# Revit family: Scale-SR_Scales-SRV947-R-IFS
name_source: partatom
category: Specialty Equipment
units: mm (PartAtom-declared; Revit-internal decimal feet)

## family parameters
Always vertical = Yes
Cut with Voids When Loaded = No
OmniClass Number = 23.40.70.11.14.11
OmniClass Title = Medical Equipment
Part Type = Normal
Room Calculation Point = No
Round Connector Dimension = Use Diameter
Shared = No
Work Plane-Based = No

## types (9) — shared parameters
Accuracy = 0.2% +/- 2 Digits of Displayed Resolution
Assembly Code = E1020810
Auto Power Down = Approximately 120 Seconds
Averaging = Automatic Digital Filter
BIM Version = v3.1
BIM Version Available (Earliest) = 2017
Calibration = Traceable to NIST Standards
Default Elevation = 0"
Display Resolution = 0.2 lb / 0.1 kg
Manufacturer = SR Scales by SR Instruments, Inc.
Maximum Weight Capacity = 400 lbs or 182 kg
Platform Depth = 24"
Power Supply = Six (6) AA 1.5 Volt Alkaline Batteries
Product Brochure Link = https://srinstruments.com
Product Page URL = https://srinstruments.com
URL = http://www.srinstruments.com
Zero = One Button Operation Auto Zero

## per-type parameters (varying)
| type | Description | Display Type | Platform Height Position | Platform Size | Platform Width | Remote Display (Not Shown Graphically) | Show Display in Platform | Show Flush Mounted Wall Display | Show Recessed Pit Frame |
| SRV947IFS | 24" x 48" Portable (or Fixed) Platform Scale with Flush Wall Mounted Display | 1.0'' LCD Display with 5 Active Digits | 0" | "24'' x 48'' x 2" (61 cm x 122 cm x 5 cm)" | 48" | No | No | Yes | Yes |
| SRV947 | 24" x 48" Portable (or Fixed) Platform Scale with Display in Platform | 1.0'' LCD Display with 5 Active Digits | 2" | "24'' x 48'' x 2" (61 cm x 122 cm x 5 cm)" | 48" | No | Yes | No | No |
| SRV947R | 24" x 48" Portable (or Fixed) Platform Scale with Remote Display | 0.75'' LCD Display with 4.5 Active Digits | 2" | "24'' x 48'' x 2" (61 cm x 122 cm x 5 cm)" | 48" | Yes | No | No | No |
| SRV945IFS | 24" x 36" Portable (or Fixed) Platform Scale with Flush Wall Mounted Display | 1.0'' LCD Display with 5 Active Digits | 0" | "24'' x 36'' x 2" (61 cm x 92 cm x 5 cm)" | 36" | No | No | Yes | Yes |
| SRV945 | 24" x 36" Portable (or Fixed) Platform Scale with Display in Platform | 1.0'' LCD Display with 5 Active Digits | 2" | "24'' x 36'' x 2" (61 cm x 92 cm x 5 cm)" | 36" | No | Yes | No | No |
| SRV945R | 24" x 36" Portable (or Fixed) Platform Scale with Remote Display | 0.75'' LCD Display with 4.5 Active Digits | 2" | "24'' x 36'' x 2" (61 cm x 92 cm x 5 cm)" | 36" | Yes | No | No | No |
| SRV949IFS | 24" x 60" Portable (or Fixed) Platform Scale with Flush Wall Mounted Display | 1.0'' LCD Display with 5 Active Digits | 0" | "24'' x 60'' x 2" (61 cm x 153 cm x 5 cm)" | 60" | No | No | Yes | Yes |
| SRV949R | 24" x 60" Portable (or Fixed) Platform Scale with Remote Display | 0.75'' LCD Display with 4.5 Active Digits | 2" | "24'' x 60'' x 2" (61 cm x 153 cm x 5 cm)" | 60" | Yes | No | No | No |
| SRV949 | 24" x 60" Portable (or Fixed) Platform Scale with Display in Platform | 1.0'' LCD Display with 5 Active Digits | 2" | "24'' x 60'' x 2" (61 cm x 153 cm x 5 cm)" | 60" | No | Yes | No | No |

note: column(s) folded — value = type name in every type: Model

## geometry (parser evidence)
native form markers: Blend x1, Sweep x3
no freeform markers — native parametric forms only
